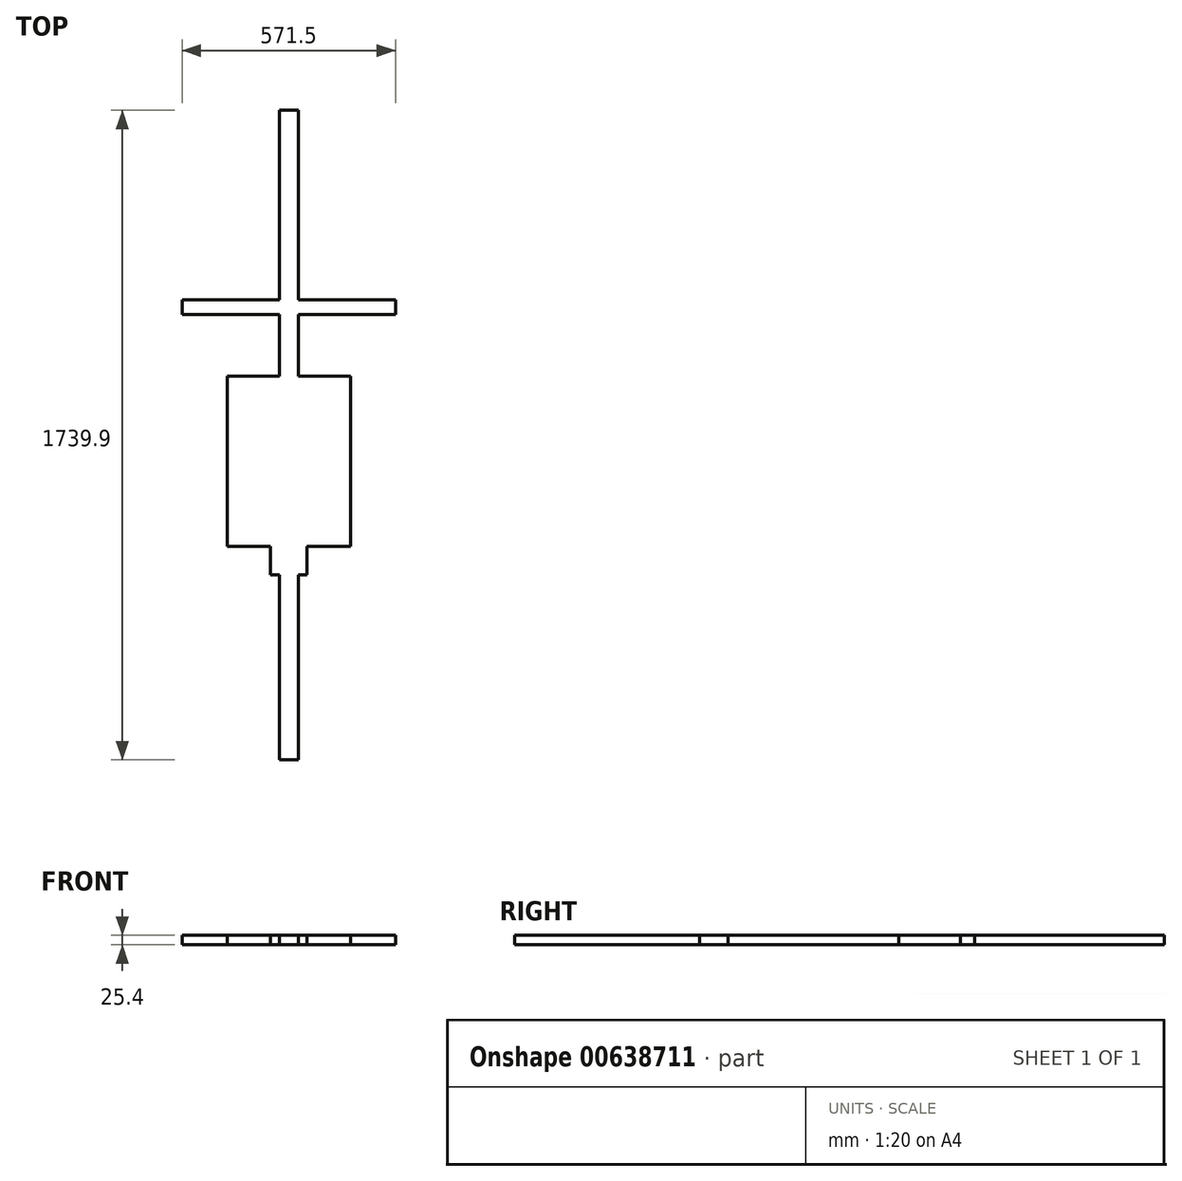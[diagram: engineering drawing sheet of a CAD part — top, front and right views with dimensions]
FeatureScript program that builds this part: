
annotation { "Feature Type Name" : "Feature", "Feature Type Description" : "" }
export const myFeature = defineFeature(function(context is Context, id is Id, definition is map)
    precondition{}
    {
        {
            var Q0;
            Q0=qCreatedBy(makeId("Top.planeOp"),FACE);
            var sketch = newSketch(context, id + "F0", { "sketchPlane" : qUnion([Q0])});
            skLineSegment(sketch, "E0.bottom", {"start": v(-25.4, 0) * mm, "end": v(25.4, 0) * mm});
            skLineSegment(sketch, "E0.top", {"start": v(-25.4, 1739.9) * mm, "end": v(25.4, 1739.9) * mm});
            skLineSegment(sketch, "E0.left", {"start": v(-25.4, 0) * mm, "end": v(-25.4, 1739.9) * mm});
            skLineSegment(sketch, "E0.right", {"start": v(25.4, 0) * mm, "end": v(25.4, 1739.9) * mm});
            skLineSegment(sketch, "E1.bottom", {"start": v(48.57, 495.3) * mm, "end": v(-48.57, 495.3) * mm});
            skLineSegment(sketch, "E1.top", {"start": v(48.57, 717.02) * mm, "end": v(-48.57, 717.02) * mm});
            skLineSegment(sketch, "E1.left", {"start": v(48.57, 495.3) * mm, "end": v(48.57, 717.02) * mm});
            skLineSegment(sketch, "E1.right", {"start": v(-48.57, 495.3) * mm, "end": v(-48.57, 717.02) * mm});
            skPoint(sketch, "E1.middle", {"position": v(0, 606.16) * mm});
            skLineSegment(sketch, "E2.bottom", {"start": v(285.75, 1193.47) * mm, "end": v(-285.75, 1193.47) * mm});
            skLineSegment(sketch, "E2.top", {"start": v(285.75, 1231.9) * mm, "end": v(-285.75, 1231.9) * mm});
            skLineSegment(sketch, "E2.left", {"start": v(285.75, 1193.47) * mm, "end": v(285.75, 1231.9) * mm});
            skLineSegment(sketch, "E2.right", {"start": v(-285.75, 1193.47) * mm, "end": v(-285.75, 1231.9) * mm});
            skPoint(sketch, "E2.middle", {"position": v(0, 1212.68) * mm});
            skLineSegment(sketch, "E3.bottom", {"start": v(165.1, 571.5) * mm, "end": v(-165.1, 571.5) * mm});
            skLineSegment(sketch, "E3.top", {"start": v(165.1, 1028.25) * mm, "end": v(-165.1, 1028.25) * mm});
            skLineSegment(sketch, "E3.left", {"start": v(165.1, 571.5) * mm, "end": v(165.1, 1028.25) * mm});
            skLineSegment(sketch, "E3.right", {"start": v(-165.1, 571.5) * mm, "end": v(-165.1, 1028.25) * mm});
            skPoint(sketch, "E3.middle", {"position": v(0, 799.87) * mm});
            skSolve(sketch);
        }
        {
            var Q0;
            Q0=qSketchRegion(id+"F0",true);
            var Q1;
            {var subQ0=sQuery(id+"F0.wireOp",EDGE,"E3.bottom");var subQ1=sQuery(id+"F0.wireOp",EDGE,"E0.left");var subQ2=makeQuery(id+"F0.imprint","INTERSECT",VERTEX,{"derivedFrom":[subQ1,subQ0]});Q1=makeQuery(id+"F0.imprint","IMPRINT",FACE,{"disambiguationData":[TD([[makeQuery(id+"F0.imprint","IMPRINT",EDGE,{"disambiguationData":[TD([[subQ2,-1.0]])],"derivedFrom":subQ1}),-1.0]])]});}
            extrude(context, id + "F1", {"entities" : qUnion([Q0, Q1]), "depth" : 25.4 * mm, "offsetDistance" : 25.4 * mm});
        }
    });
